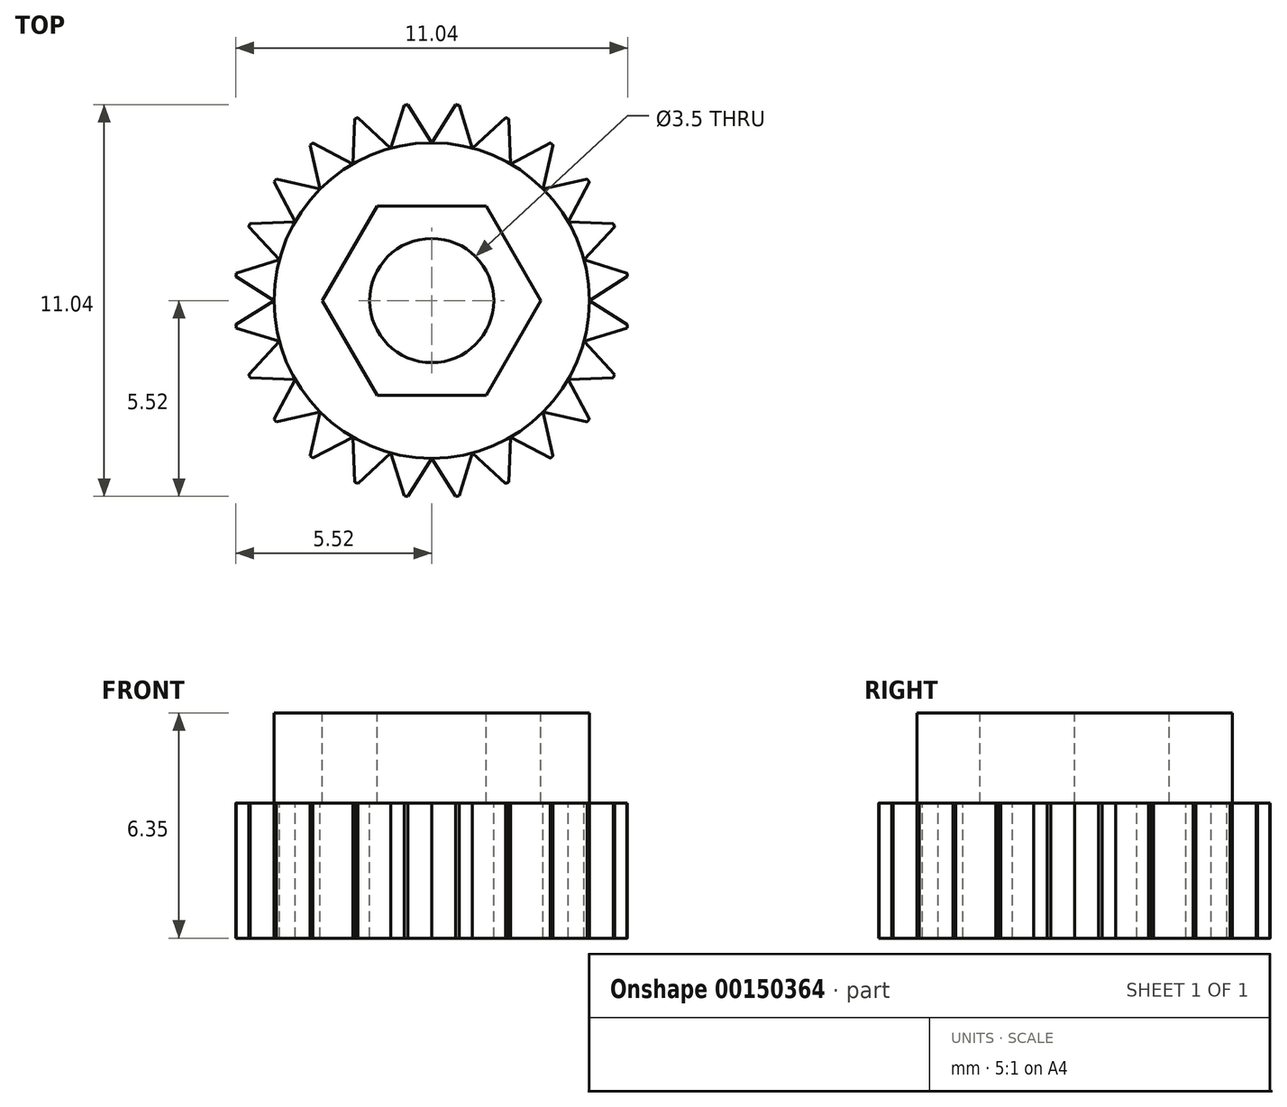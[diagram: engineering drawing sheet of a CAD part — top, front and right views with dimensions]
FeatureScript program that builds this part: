
annotation { "Feature Type Name" : "Feature", "Feature Type Description" : "" }
export const myFeature = defineFeature(function(context is Context, id is Id, definition is map)
    precondition{}
    {
        {
            var Q0;
            Q0=qCreatedBy(makeId("Front.planeOp"),FACE);
            var sketch = newSketch(context, id + "F0", { "sketchPlane" : qUnion([Q0])});
            skLineSegment(sketch, "E0", {"start": v(0, 0) * mm, "end": v(0, -6.35) * mm, "construction": true});
            skLineSegment(sketch, "E1", {"start": v(-1.75, -6.35) * mm, "end": v(-5.56, -6.35) * mm});
            skLineSegment(sketch, "E2", {"start": v(-5.56, -6.35) * mm, "end": v(-5.56, -2.54) * mm});
            skLineSegment(sketch, "E3", {"start": v(-5.56, -2.54) * mm, "end": v(-4.45, -2.54) * mm});
            skLineSegment(sketch, "E4", {"start": v(-4.45, -2.54) * mm, "end": v(-4.45, 0) * mm});
            skLineSegment(sketch, "E5", {"start": v(-4.45, 0) * mm, "end": v(-1.75, 0) * mm});
            skLineSegment(sketch, "E6", {"start": v(-1.75, -6.35) * mm, "end": v(-1.75, 0) * mm});
            skSolve(sketch);
        }
        {
            var Q0;
            Q0 = qSketchRegion(id + "F0", true);
            var Q1;
            Q1=sQuery(id+"F0.wireOp",EDGE,"E0");
            revolve(context, id + "F1", {"entities" : qUnion([Q0]), "axis" : qUnion([Q1]), "revolveType" : RevolveType.FULL});
        }
        {
            var Q0;
            Q0=makeQuery(id+"F1.opRevolve","SWEPT_FACE",FACE,{"disambiguationData":[OSD([sQuery(id+"F0.wireOp",EDGE,"E5")])]});
            var sketch = newSketch(context, id + "F2", { "sketchPlane" : qUnion([Q0])});
            skCircle(sketch, "E7.cCircle", {"center": v(0, 0) * mm, "radius": 2.67 * mm, "construction": true});
            skLineSegment(sketch, "E7.0", {"start": v(-1.54, 2.67) * mm, "end": v(1.54, 2.67) * mm});
            skLineSegment(sketch, "E7.1", {"start": v(1.54, 2.67) * mm, "end": v(3.08, 0) * mm});
            skLineSegment(sketch, "E7.2", {"start": v(3.08, 0) * mm, "end": v(1.54, -2.67) * mm});
            skLineSegment(sketch, "E7.3", {"start": v(1.54, -2.67) * mm, "end": v(-1.54, -2.67) * mm});
            skLineSegment(sketch, "E7.4", {"start": v(-1.54, -2.67) * mm, "end": v(-3.08, 0) * mm});
            skLineSegment(sketch, "E7.5", {"start": v(-3.08, 0) * mm, "end": v(-1.54, 2.67) * mm});
            skPoint(sketch, "E7.0.midPoint", {"position": v(0, 2.67) * mm});
            skSolve(sketch);
        }
        {
            var Q0;
            Q0 = qSketchRegion(id + "F2", true);
            extrude(context, id + "F3", {"entities" : qUnion([Q0]), "operationType" : NewBodyOperationType.REMOVE, "oppositeDirection" : true, "depth" : 2.54 * mm});
        }
        {
            var Q0;
            Q0=makeQuery(id+"F1.opRevolve","SWEPT_FACE",FACE,{"disambiguationData":[OSD([sQuery(id+"F0.wireOp",EDGE,"E3")])]});
            var sketch = newSketch(context, id + "F4", { "sketchPlane" : qUnion([Q0])});
            skLineSegment(sketch, "E8", {"start": v(0, 4.45) * mm, "end": v(-0.68, 5.52) * mm});
            skLineSegment(sketch, "E9", {"start": v(0, 4.45) * mm, "end": v(0.68, 5.52) * mm});
            skCircle(sketch, "E10", {"center": v(0, 0) * mm, "radius": 6.67 * mm});
            skArc(sketch, "E11.0", {"start": v(-0.68, 5.52) * mm, "mid": v(-0.73, 5.51) * mm, "end": v(-0.77, 5.5) * mm});
            skPoint(sketch, "E12.start.orphan", {"position": v(0, 5.56) * mm});
            skLineSegment(sketch, "E13", {"start": v(0, 5.56) * mm, "end": v(-0.68, 5.52) * mm, "construction": true});
            skLineSegment(sketch, "E14", {"start": v(0, 5.56) * mm, "end": v(0.68, 5.52) * mm, "construction": true});
            skLineSegment(sketch, "E15.1.0", {"start": v(-1.15, 4.3) * mm, "end": v(-2.08, 5.16) * mm});
            skLineSegment(sketch, "E15.1.1", {"start": v(-1.15, 4.3) * mm, "end": v(-0.77, 5.5) * mm});
            skLineSegment(sketch, "E15.2.0", {"start": v(-2.22, 3.85) * mm, "end": v(-3.35, 4.44) * mm});
            skLineSegment(sketch, "E15.2.1", {"start": v(-2.22, 3.85) * mm, "end": v(-2.17, 5.12) * mm});
            skLineSegment(sketch, "E15.3.0", {"start": v(-3.14, 3.14) * mm, "end": v(-4.38, 3.42) * mm});
            skLineSegment(sketch, "E15.3.1", {"start": v(-3.14, 3.14) * mm, "end": v(-3.42, 4.38) * mm});
            skLineSegment(sketch, "E15.4.0", {"start": v(-3.85, 2.22) * mm, "end": v(-5.12, 2.17) * mm});
            skLineSegment(sketch, "E15.4.1", {"start": v(-3.85, 2.22) * mm, "end": v(-4.44, 3.35) * mm});
            skLineSegment(sketch, "E15.5.0", {"start": v(-4.3, 1.15) * mm, "end": v(-5.5, 0.77) * mm});
            skLineSegment(sketch, "E15.5.1", {"start": v(-4.3, 1.15) * mm, "end": v(-5.16, 2.08) * mm});
            skLineSegment(sketch, "E15.6.0", {"start": v(-4.45, 0) * mm, "end": v(-5.52, -0.68) * mm});
            skLineSegment(sketch, "E15.6.1", {"start": v(-4.45, 0) * mm, "end": v(-5.52, 0.68) * mm});
            skLineSegment(sketch, "E15.7.0", {"start": v(-4.3, -1.15) * mm, "end": v(-5.16, -2.08) * mm});
            skLineSegment(sketch, "E15.7.1", {"start": v(-4.3, -1.15) * mm, "end": v(-5.5, -0.77) * mm});
            skLineSegment(sketch, "E15.8.0", {"start": v(-3.85, -2.22) * mm, "end": v(-4.44, -3.35) * mm});
            skLineSegment(sketch, "E15.8.1", {"start": v(-3.85, -2.22) * mm, "end": v(-5.12, -2.17) * mm});
            skLineSegment(sketch, "E15.9.0", {"start": v(-3.14, -3.14) * mm, "end": v(-3.42, -4.38) * mm});
            skLineSegment(sketch, "E15.9.1", {"start": v(-3.14, -3.14) * mm, "end": v(-4.38, -3.42) * mm});
            skLineSegment(sketch, "E15.10.0", {"start": v(-2.22, -3.85) * mm, "end": v(-2.17, -5.12) * mm});
            skLineSegment(sketch, "E15.10.1", {"start": v(-2.22, -3.85) * mm, "end": v(-3.35, -4.44) * mm});
            skLineSegment(sketch, "E15.11.0", {"start": v(-1.15, -4.3) * mm, "end": v(-0.77, -5.5) * mm});
            skLineSegment(sketch, "E15.11.1", {"start": v(-1.15, -4.3) * mm, "end": v(-2.08, -5.16) * mm});
            skLineSegment(sketch, "E15.12.0", {"start": v(0, -4.45) * mm, "end": v(0.68, -5.52) * mm});
            skLineSegment(sketch, "E15.12.1", {"start": v(0, -4.45) * mm, "end": v(-0.68, -5.52) * mm});
            skLineSegment(sketch, "E15.13.0", {"start": v(1.15, -4.3) * mm, "end": v(2.08, -5.16) * mm});
            skLineSegment(sketch, "E15.13.1", {"start": v(1.15, -4.3) * mm, "end": v(0.77, -5.5) * mm});
            skLineSegment(sketch, "E15.14.0", {"start": v(2.22, -3.85) * mm, "end": v(3.35, -4.44) * mm});
            skLineSegment(sketch, "E15.14.1", {"start": v(2.22, -3.85) * mm, "end": v(2.17, -5.12) * mm});
            skLineSegment(sketch, "E15.15.0", {"start": v(3.14, -3.14) * mm, "end": v(4.38, -3.42) * mm});
            skLineSegment(sketch, "E15.15.1", {"start": v(3.14, -3.14) * mm, "end": v(3.42, -4.38) * mm});
            skLineSegment(sketch, "E15.16.0", {"start": v(3.85, -2.22) * mm, "end": v(5.12, -2.17) * mm});
            skLineSegment(sketch, "E15.16.1", {"start": v(3.85, -2.22) * mm, "end": v(4.44, -3.35) * mm});
            skLineSegment(sketch, "E15.17.0", {"start": v(4.3, -1.15) * mm, "end": v(5.5, -0.77) * mm});
            skLineSegment(sketch, "E15.17.1", {"start": v(4.3, -1.15) * mm, "end": v(5.16, -2.08) * mm});
            skLineSegment(sketch, "E15.18.0", {"start": v(4.45, 0) * mm, "end": v(5.52, 0.68) * mm});
            skLineSegment(sketch, "E15.18.1", {"start": v(4.45, 0) * mm, "end": v(5.52, -0.68) * mm});
            skLineSegment(sketch, "E15.19.0", {"start": v(4.3, 1.15) * mm, "end": v(5.16, 2.08) * mm});
            skLineSegment(sketch, "E15.19.1", {"start": v(4.3, 1.15) * mm, "end": v(5.5, 0.77) * mm});
            skLineSegment(sketch, "E15.20.0", {"start": v(3.85, 2.22) * mm, "end": v(4.44, 3.35) * mm});
            skLineSegment(sketch, "E15.20.1", {"start": v(3.85, 2.22) * mm, "end": v(5.12, 2.17) * mm});
            skLineSegment(sketch, "E15.21.0", {"start": v(3.14, 3.14) * mm, "end": v(3.42, 4.38) * mm});
            skLineSegment(sketch, "E15.21.1", {"start": v(3.14, 3.14) * mm, "end": v(4.38, 3.42) * mm});
            skLineSegment(sketch, "E15.22.0", {"start": v(2.22, 3.85) * mm, "end": v(2.17, 5.12) * mm});
            skLineSegment(sketch, "E15.22.1", {"start": v(2.22, 3.85) * mm, "end": v(3.35, 4.44) * mm});
            skLineSegment(sketch, "E15.23.0", {"start": v(1.15, 4.3) * mm, "end": v(0.77, 5.5) * mm});
            skLineSegment(sketch, "E15.23.1", {"start": v(1.15, 4.3) * mm, "end": v(2.08, 5.16) * mm});
            skArc(sketch, "E16.trimOffspring", {"start": v(-2.08, 5.16) * mm, "mid": v(-2.13, 5.14) * mm, "end": v(-2.17, 5.12) * mm});
            skArc(sketch, "E17.trimOffspring", {"start": v(-3.35, 4.44) * mm, "mid": v(-3.38, 4.41) * mm, "end": v(-3.42, 4.38) * mm});
            skArc(sketch, "E18.trimOffspring", {"start": v(-4.38, 3.42) * mm, "mid": v(-4.41, 3.38) * mm, "end": v(-4.44, 3.35) * mm});
            skArc(sketch, "E19.trimOffspring", {"start": v(-5.12, 2.17) * mm, "mid": v(-5.14, 2.13) * mm, "end": v(-5.16, 2.08) * mm});
            skArc(sketch, "E20.trimOffspring", {"start": v(-5.5, 0.77) * mm, "mid": v(-5.51, 0.73) * mm, "end": v(-5.52, 0.68) * mm});
            skArc(sketch, "E21.trimOffspring", {"start": v(-5.52, -0.68) * mm, "mid": v(-5.51, -0.73) * mm, "end": v(-5.5, -0.77) * mm});
            skArc(sketch, "E22.trimOffspring", {"start": v(-5.16, -2.08) * mm, "mid": v(-5.14, -2.13) * mm, "end": v(-5.12, -2.17) * mm});
            skArc(sketch, "E23.trimOffspring", {"start": v(-4.44, -3.35) * mm, "mid": v(-4.41, -3.38) * mm, "end": v(-4.38, -3.42) * mm});
            skArc(sketch, "E24.trimOffspring", {"start": v(-3.42, -4.38) * mm, "mid": v(-3.38, -4.41) * mm, "end": v(-3.35, -4.44) * mm});
            skArc(sketch, "E25.trimOffspring", {"start": v(-2.17, -5.12) * mm, "mid": v(-2.13, -5.14) * mm, "end": v(-2.08, -5.16) * mm});
            skArc(sketch, "E26.trimOffspring", {"start": v(0.68, -5.52) * mm, "mid": v(0.73, -5.51) * mm, "end": v(0.77, -5.5) * mm});
            skArc(sketch, "E27.trimOffspring", {"start": v(2.08, -5.16) * mm, "mid": v(2.13, -5.14) * mm, "end": v(2.17, -5.12) * mm});
            skArc(sketch, "E28.trimOffspring", {"start": v(3.35, -4.44) * mm, "mid": v(3.38, -4.41) * mm, "end": v(3.42, -4.38) * mm});
            skArc(sketch, "E29.trimOffspring", {"start": v(4.38, -3.42) * mm, "mid": v(4.41, -3.38) * mm, "end": v(4.44, -3.35) * mm});
            skArc(sketch, "E30.trimOffspring", {"start": v(5.12, -2.17) * mm, "mid": v(5.14, -2.13) * mm, "end": v(5.16, -2.08) * mm});
            skArc(sketch, "E31.trimOffspring", {"start": v(5.5, -0.77) * mm, "mid": v(5.51, -0.73) * mm, "end": v(5.52, -0.68) * mm});
            skArc(sketch, "E32.trimOffspring", {"start": v(5.52, 0.68) * mm, "mid": v(5.51, 0.73) * mm, "end": v(5.5, 0.77) * mm});
            skArc(sketch, "E33.trimOffspring", {"start": v(5.16, 2.08) * mm, "mid": v(5.14, 2.13) * mm, "end": v(5.12, 2.17) * mm});
            skArc(sketch, "E34.trimOffspring", {"start": v(4.44, 3.35) * mm, "mid": v(4.41, 3.38) * mm, "end": v(4.38, 3.42) * mm});
            skArc(sketch, "E35.trimOffspring", {"start": v(3.42, 4.38) * mm, "mid": v(3.38, 4.41) * mm, "end": v(3.35, 4.44) * mm});
            skArc(sketch, "E36.trimOffspring", {"start": v(2.17, 5.12) * mm, "mid": v(2.13, 5.14) * mm, "end": v(2.08, 5.16) * mm});
            skArc(sketch, "E37.trimOffspring", {"start": v(0.77, 5.5) * mm, "mid": v(0.73, 5.51) * mm, "end": v(0.68, 5.52) * mm});
            skSolve(sketch);
        }
        {
            var Q0;
            {var subQ0=sQuery(id+"F4.wireOp",EDGE,"E15.4.0");Q0=makeQuery(id+"F4.imprint","IMPRINT",FACE,{"disambiguationData":[TD([[makeQuery(id+"F4.imprint","IMPRINT",EDGE,{"derivedFrom":subQ0}),-1.0]])]});}
            var Q1;
            Q1=makeQuery(id+"F4.imprint","IMPRINT",FACE,{"disambiguationData":[TD([[makeQuery(id+"F4.imprint","IMPRINT",EDGE,{"derivedFrom":sQuery(id+"F4.wireOp",EDGE,"E10")}),1.0]])]});
            var Q2;
            {var subQ0=sQuery(id+"F4.wireOp",EDGE,"E15.3.0");Q2=makeQuery(id+"F4.imprint","IMPRINT",FACE,{"disambiguationData":[TD([[makeQuery(id+"F4.imprint","IMPRINT",EDGE,{"derivedFrom":subQ0}),-1.0]])]});}
            var Q3;
            {var subQ0=sQuery(id+"F4.wireOp",EDGE,"E15.2.0");Q3=makeQuery(id+"F4.imprint","IMPRINT",FACE,{"disambiguationData":[TD([[makeQuery(id+"F4.imprint","IMPRINT",EDGE,{"derivedFrom":subQ0}),-1.0]])]});}
            var Q4;
            {var subQ0=sQuery(id+"F4.wireOp",EDGE,"E15.1.0");Q4=makeQuery(id+"F4.imprint","IMPRINT",FACE,{"disambiguationData":[TD([[makeQuery(id+"F4.imprint","IMPRINT",EDGE,{"derivedFrom":subQ0}),-1.0]])]});}
            var Q5;
            {var subQ0=sQuery(id+"F4.wireOp",EDGE,"E15.5.0");Q5=makeQuery(id+"F4.imprint","IMPRINT",FACE,{"disambiguationData":[TD([[makeQuery(id+"F4.imprint","IMPRINT",EDGE,{"derivedFrom":subQ0}),-1.0]])]});}
            var Q6;
            {var subQ0=sQuery(id+"F4.wireOp",EDGE,"E15.6.0");Q6=makeQuery(id+"F4.imprint","IMPRINT",FACE,{"disambiguationData":[TD([[makeQuery(id+"F4.imprint","IMPRINT",EDGE,{"derivedFrom":subQ0}),-1.0]])]});}
            var Q7;
            {var subQ0=sQuery(id+"F4.wireOp",EDGE,"E15.7.0");Q7=makeQuery(id+"F4.imprint","IMPRINT",FACE,{"disambiguationData":[TD([[makeQuery(id+"F4.imprint","IMPRINT",EDGE,{"derivedFrom":subQ0}),-1.0]])]});}
            var Q8;
            {var subQ0=sQuery(id+"F4.wireOp",EDGE,"E15.8.0");Q8=makeQuery(id+"F4.imprint","IMPRINT",FACE,{"disambiguationData":[TD([[makeQuery(id+"F4.imprint","IMPRINT",EDGE,{"derivedFrom":subQ0}),-1.0]])]});}
            var Q9;
            {var subQ0=sQuery(id+"F4.wireOp",EDGE,"E15.9.0");Q9=makeQuery(id+"F4.imprint","IMPRINT",FACE,{"disambiguationData":[TD([[makeQuery(id+"F4.imprint","IMPRINT",EDGE,{"derivedFrom":subQ0}),-1.0]])]});}
            var Q10;
            {var subQ0=sQuery(id+"F4.wireOp",EDGE,"E15.10.0");Q10=makeQuery(id+"F4.imprint","IMPRINT",FACE,{"disambiguationData":[TD([[makeQuery(id+"F4.imprint","IMPRINT",EDGE,{"derivedFrom":subQ0}),-1.0]])]});}
            var Q11;
            {var subQ0=sQuery(id+"F4.wireOp",EDGE,"E15.11.0");Q11=makeQuery(id+"F4.imprint","IMPRINT",FACE,{"disambiguationData":[TD([[makeQuery(id+"F4.imprint","IMPRINT",EDGE,{"derivedFrom":subQ0}),-1.0]])]});}
            var Q12;
            {var subQ0=sQuery(id+"F4.wireOp",EDGE,"E15.12.0");Q12=makeQuery(id+"F4.imprint","IMPRINT",FACE,{"disambiguationData":[TD([[makeQuery(id+"F4.imprint","IMPRINT",EDGE,{"derivedFrom":subQ0}),-1.0]])]});}
            var Q13;
            {var subQ0=sQuery(id+"F4.wireOp",EDGE,"E15.13.0");Q13=makeQuery(id+"F4.imprint","IMPRINT",FACE,{"disambiguationData":[TD([[makeQuery(id+"F4.imprint","IMPRINT",EDGE,{"derivedFrom":subQ0}),-1.0]])]});}
            var Q14;
            {var subQ0=sQuery(id+"F4.wireOp",EDGE,"E15.14.0");Q14=makeQuery(id+"F4.imprint","IMPRINT",FACE,{"disambiguationData":[TD([[makeQuery(id+"F4.imprint","IMPRINT",EDGE,{"derivedFrom":subQ0}),-1.0]])]});}
            var Q15;
            {var subQ0=sQuery(id+"F4.wireOp",EDGE,"E15.15.0");Q15=makeQuery(id+"F4.imprint","IMPRINT",FACE,{"disambiguationData":[TD([[makeQuery(id+"F4.imprint","IMPRINT",EDGE,{"derivedFrom":subQ0}),-1.0]])]});}
            var Q16;
            {var subQ0=sQuery(id+"F4.wireOp",EDGE,"E15.16.0");Q16=makeQuery(id+"F4.imprint","IMPRINT",FACE,{"disambiguationData":[TD([[makeQuery(id+"F4.imprint","IMPRINT",EDGE,{"derivedFrom":subQ0}),-1.0]])]});}
            var Q17;
            {var subQ0=sQuery(id+"F4.wireOp",EDGE,"E15.17.0");Q17=makeQuery(id+"F4.imprint","IMPRINT",FACE,{"disambiguationData":[TD([[makeQuery(id+"F4.imprint","IMPRINT",EDGE,{"derivedFrom":subQ0}),-1.0]])]});}
            var Q18;
            {var subQ0=sQuery(id+"F4.wireOp",EDGE,"E15.18.0");Q18=makeQuery(id+"F4.imprint","IMPRINT",FACE,{"disambiguationData":[TD([[makeQuery(id+"F4.imprint","IMPRINT",EDGE,{"derivedFrom":subQ0}),-1.0]])]});}
            var Q19;
            {var subQ0=sQuery(id+"F4.wireOp",EDGE,"E15.19.0");Q19=makeQuery(id+"F4.imprint","IMPRINT",FACE,{"disambiguationData":[TD([[makeQuery(id+"F4.imprint","IMPRINT",EDGE,{"derivedFrom":subQ0}),-1.0]])]});}
            var Q20;
            {var subQ0=sQuery(id+"F4.wireOp",EDGE,"E15.20.0");Q20=makeQuery(id+"F4.imprint","IMPRINT",FACE,{"disambiguationData":[TD([[makeQuery(id+"F4.imprint","IMPRINT",EDGE,{"derivedFrom":subQ0}),-1.0]])]});}
            var Q21;
            {var subQ0=sQuery(id+"F4.wireOp",EDGE,"E15.21.0");Q21=makeQuery(id+"F4.imprint","IMPRINT",FACE,{"disambiguationData":[TD([[makeQuery(id+"F4.imprint","IMPRINT",EDGE,{"derivedFrom":subQ0}),-1.0]])]});}
            var Q22;
            {var subQ0=sQuery(id+"F4.wireOp",EDGE,"E15.22.0");Q22=makeQuery(id+"F4.imprint","IMPRINT",FACE,{"disambiguationData":[TD([[makeQuery(id+"F4.imprint","IMPRINT",EDGE,{"derivedFrom":subQ0}),-1.0]])]});}
            var Q23;
            {var subQ0=sQuery(id+"F4.wireOp",EDGE,"E15.23.0");Q23=makeQuery(id+"F4.imprint","IMPRINT",FACE,{"disambiguationData":[TD([[makeQuery(id+"F4.imprint","IMPRINT",EDGE,{"derivedFrom":subQ0}),-1.0]])]});}
            var Q24;
            {var subQ0=sQuery(id+"F4.wireOp",EDGE,"E8");Q24=makeQuery(id+"F4.imprint","IMPRINT",FACE,{"disambiguationData":[TD([[makeQuery(id+"F4.imprint","IMPRINT",EDGE,{"derivedFrom":subQ0}),-1.0]])]});}
            extrude(context, id + "F5", {"entities" : qUnion([Q0, Q1, Q2, Q3, Q4, Q5, Q6, Q7, Q8, Q9, Q10, Q11, Q12, Q13, Q14, Q15, Q16, Q17, Q18, Q19, Q20, Q21, Q22, Q23, Q24]), "operationType" : NewBodyOperationType.REMOVE, "oppositeDirection" : true, "depth" : 25.4 * mm});
        }
    });
